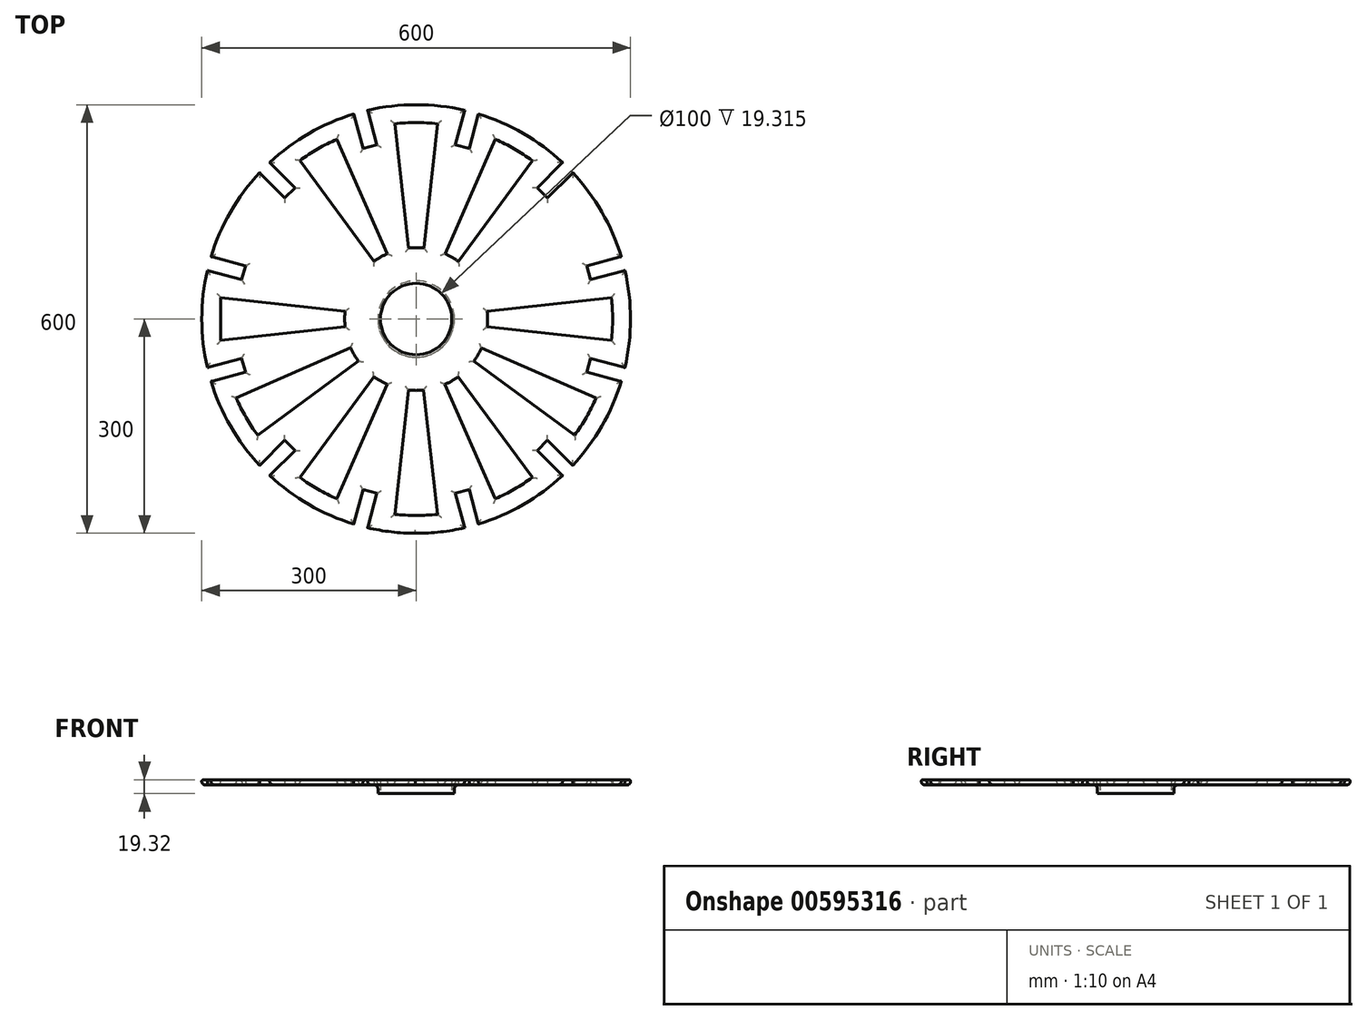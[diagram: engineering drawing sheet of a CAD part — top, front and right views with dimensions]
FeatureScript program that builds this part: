
annotation { "Feature Type Name" : "Feature", "Feature Type Description" : "" }
export const myFeature = defineFeature(function(context is Context, id is Id, definition is map)
    precondition{}
    {
        {
            var Q0;
            Q0=qCreatedBy(makeId("Right.planeOp"),FACE);
            var sketch = newSketch(context, id + "F0", { "sketchPlane" : qUnion([Q0])});
            skLineSegment(sketch, "E0.bottom", {"start": v(0, 0) * mm, "end": v(-300, 0) * mm});
            skLineSegment(sketch, "E0.top", {"start": v(0, 7) * mm, "end": v(-300, 7) * mm});
            skLineSegment(sketch, "E0.left", {"start": v(0, 0) * mm, "end": v(0, 7) * mm});
            skLineSegment(sketch, "E0.right", {"start": v(-300, 0) * mm, "end": v(-300, 7) * mm});
            skSolve(sketch);
        }
        {
            var Q0;
            Q0=makeQuery(id+"F0.imprint","IMPRINT",FACE,{"disambiguationData":[TD([[makeQuery(id+"F0.imprint","IMPRINT",EDGE,{"derivedFrom":sQuery(id+"F0.wireOp",EDGE,"E0.bottom")}),-1.0]])]});
            extrude(context, id + "F1", {"entities" : qUnion([Q0]), "oppositeDirection" : true, "depth" : 1 * mm, "offsetDistance" : 25 * mm});
        }
        {
            var Q0;
            Q0=qCreatedBy(makeId("Right.planeOp"),FACE);
            var sketch = newSketch(context, id + "F2", { "sketchPlane" : qUnion([Q0])});
            skLineSegment(sketch, "E1", {"start": v(-250.92, 0) * mm, "end": v(-210.92, 0) * mm});
            skLineSegment(sketch, "E2", {"start": v(-250.92, 0) * mm, "end": v(-250.92, 7.32) * mm});
            skLineSegment(sketch, "E3", {"start": v(-250.92, 7.32) * mm, "end": v(-210.92, 7.32) * mm});
            skLineSegment(sketch, "E4", {"start": v(-210.92, 7.32) * mm, "end": v(-210.92, 0) * mm});
            skLineSegment(sketch, "E5", {"start": v(0, 0) * mm, "end": v(-300, 0) * mm});
            skLineSegment(sketch, "E6", {"start": v(-300, 0) * mm, "end": v(-300, 7.32) * mm});
            skLineSegment(sketch, "E7", {"start": v(-300, 7.32) * mm, "end": v(0, 7.32) * mm});
            skLineSegment(sketch, "E8", {"start": v(0, 7.32) * mm, "end": v(0, 0) * mm});
            skSolve(sketch);
        }
        {
            var Q0;
            {var subQ0=sQuery(id+"F2.wireOp",EDGE,"E2");Q0=makeQuery(id+"F2.imprint","IMPRINT",FACE,{"disambiguationData":[TD([[makeQuery(id+"F2.imprint","IMPRINT",EDGE,{"derivedFrom":subQ0}),1.0]])]});}
            var Q1;
            {var subQ0=sQuery(id+"F2.wireOp",EDGE,"E4");Q1=makeQuery(id+"F2.imprint","IMPRINT",FACE,{"disambiguationData":[TD([[makeQuery(id+"F2.imprint","IMPRINT",EDGE,{"derivedFrom":subQ0}),1.0]])]});}
            var Q2;
            {var subQ0=sQuery(id+"F2.wireOp",EDGE,"E2");Q2=makeQuery(id+"F2.imprint","IMPRINT",FACE,{"disambiguationData":[TD([[makeQuery(id+"F2.imprint","IMPRINT",EDGE,{"derivedFrom":subQ0}),-1.0]])]});}
            var Q3;
            Q3=sQuery(id+"F2.wireOp",EDGE,"E8");
            revolve(context, id + "F3", {"operationType" : NewBodyOperationType.ADD, "entities" : qUnion([Q0, Q1, Q2]), "axis" : qUnion([Q3]), "revolveType" : RevolveType.FULL});
        }
        {
            var Q0;
            Q0=makeQuery(id+"F3.opRevolve","SWEPT_EDGE",EDGE,{"disambiguationData":[OSD([sQuery(id+"F2.wireOp",EDGE,"E6"),sQuery(id+"F2.wireOp",EDGE,"E7")])]});
            fillet(context, id + "F4", {"entities" : qUnion([Q0]), "radius" : 2 * mm, "tangentPropagation" : true, "allowEdgeOverflow" : false});
        }
        {
            var Q0;
            Q0=qCreatedBy(makeId("Top.planeOp"),FACE);
            var sketch = newSketch(context, id + "F5", { "sketchPlane" : qUnion([Q0])});
            skCircle(sketch, "E9.cCircle", {"center": v(0, 0) * mm, "radius": 300.17 * mm, "construction": true});
            skLineSegment(sketch, "E9.0", {"start": v(80.43, -300.17) * mm, "end": v(-80.43, -300.17) * mm});
            skLineSegment(sketch, "E9.1", {"start": v(-80.43, -300.17) * mm, "end": v(-219.74, -219.74) * mm});
            skLineSegment(sketch, "E9.2", {"start": v(-219.74, -219.74) * mm, "end": v(-300.17, -80.43) * mm});
            skLineSegment(sketch, "E9.3", {"start": v(-300.17, -80.43) * mm, "end": v(-300.17, 80.43) * mm});
            skLineSegment(sketch, "E9.4", {"start": v(-300.17, 80.43) * mm, "end": v(-219.74, 219.74) * mm});
            skLineSegment(sketch, "E9.5", {"start": v(-219.74, 219.74) * mm, "end": v(-80.43, 300.17) * mm});
            skLineSegment(sketch, "E9.6", {"start": v(-80.43, 300.17) * mm, "end": v(80.43, 300.17) * mm});
            skLineSegment(sketch, "E9.7", {"start": v(80.43, 300.17) * mm, "end": v(219.74, 219.74) * mm});
            skLineSegment(sketch, "E9.8", {"start": v(219.74, 219.74) * mm, "end": v(300.17, 80.43) * mm});
            skLineSegment(sketch, "E9.9", {"start": v(300.17, 80.43) * mm, "end": v(300.17, -80.43) * mm});
            skLineSegment(sketch, "E9.10", {"start": v(300.17, -80.43) * mm, "end": v(219.74, -219.74) * mm});
            skLineSegment(sketch, "E9.11", {"start": v(219.74, -219.74) * mm, "end": v(80.43, -300.17) * mm});
            skLineSegment(sketch, "E10", {"start": v(-80.43, -300.17) * mm, "end": v(80.43, 300.17) * mm});
            skLineSegment(sketch, "E11", {"start": v(-80.43, 300.17) * mm, "end": v(80.43, -300.17) * mm});
            skLineSegment(sketch, "E12", {"start": v(219.74, -219.74) * mm, "end": v(-219.74, 219.74) * mm});
            skLineSegment(sketch, "E13", {"start": v(219.74, 219.74) * mm, "end": v(-219.74, -219.74) * mm});
            skLineSegment(sketch, "E14", {"start": v(-300.17, -80.43) * mm, "end": v(300.17, 80.43) * mm});
            skLineSegment(sketch, "E15", {"start": v(300.17, -80.43) * mm, "end": v(-300.17, 80.43) * mm});
            skLineSegment(sketch, "E16", {"start": v(-87.3, 287.19) * mm, "end": v(-67.99, 292.37) * mm});
            skLineSegment(sketch, "E17", {"start": v(-87.3, 287.19) * mm, "end": v(-74.36, 238.9) * mm});
            skLineSegment(sketch, "E18", {"start": v(-74.36, 238.9) * mm, "end": v(-55.05, 244.07) * mm});
            skLineSegment(sketch, "E19", {"start": v(-55.05, 244.07) * mm, "end": v(-67.99, 292.37) * mm});
            skLineSegment(sketch, "E20.1.0", {"start": v(67.99, 292.37) * mm, "end": v(55.05, 244.07) * mm});
            skLineSegment(sketch, "E20.1.1", {"start": v(74.36, 238.9) * mm, "end": v(87.3, 287.19) * mm});
            skLineSegment(sketch, "E20.1.2", {"start": v(55.05, 244.07) * mm, "end": v(74.36, 238.9) * mm});
            skLineSegment(sketch, "E20.1.3", {"start": v(67.99, 292.37) * mm, "end": v(87.3, 287.19) * mm});
            skLineSegment(sketch, "E20.2.0", {"start": v(205.06, 219.2) * mm, "end": v(169.7, 183.85) * mm});
            skLineSegment(sketch, "E20.2.1", {"start": v(183.85, 169.7) * mm, "end": v(219.2, 205.06) * mm});
            skLineSegment(sketch, "E20.2.2", {"start": v(169.7, 183.85) * mm, "end": v(183.85, 169.7) * mm});
            skLineSegment(sketch, "E20.2.3", {"start": v(205.06, 219.2) * mm, "end": v(219.2, 205.06) * mm});
            skLineSegment(sketch, "E20.3.0", {"start": v(287.19, 87.3) * mm, "end": v(238.9, 74.36) * mm});
            skLineSegment(sketch, "E20.3.1", {"start": v(244.07, 55.05) * mm, "end": v(292.37, 67.99) * mm});
            skLineSegment(sketch, "E20.3.2", {"start": v(238.9, 74.36) * mm, "end": v(244.07, 55.05) * mm});
            skLineSegment(sketch, "E20.3.3", {"start": v(287.19, 87.3) * mm, "end": v(292.37, 67.99) * mm});
            skLineSegment(sketch, "E20.4.0", {"start": v(292.37, -67.99) * mm, "end": v(244.07, -55.05) * mm});
            skLineSegment(sketch, "E20.4.1", {"start": v(238.9, -74.36) * mm, "end": v(287.19, -87.3) * mm});
            skLineSegment(sketch, "E20.4.2", {"start": v(244.07, -55.05) * mm, "end": v(238.9, -74.36) * mm});
            skLineSegment(sketch, "E20.4.3", {"start": v(292.37, -67.99) * mm, "end": v(287.19, -87.3) * mm});
            skLineSegment(sketch, "E20.5.0", {"start": v(219.2, -205.06) * mm, "end": v(183.85, -169.7) * mm});
            skLineSegment(sketch, "E20.5.1", {"start": v(169.7, -183.85) * mm, "end": v(205.06, -219.2) * mm});
            skLineSegment(sketch, "E20.5.2", {"start": v(183.85, -169.7) * mm, "end": v(169.7, -183.85) * mm});
            skLineSegment(sketch, "E20.5.3", {"start": v(219.2, -205.06) * mm, "end": v(205.06, -219.2) * mm});
            skLineSegment(sketch, "E20.6.0", {"start": v(87.3, -287.19) * mm, "end": v(74.36, -238.9) * mm});
            skLineSegment(sketch, "E20.6.1", {"start": v(55.05, -244.07) * mm, "end": v(67.99, -292.37) * mm});
            skLineSegment(sketch, "E20.6.2", {"start": v(74.36, -238.9) * mm, "end": v(55.05, -244.07) * mm});
            skLineSegment(sketch, "E20.6.3", {"start": v(87.3, -287.19) * mm, "end": v(67.99, -292.37) * mm});
            skLineSegment(sketch, "E20.7.0", {"start": v(-67.99, -292.37) * mm, "end": v(-55.05, -244.07) * mm});
            skLineSegment(sketch, "E20.7.1", {"start": v(-74.36, -238.9) * mm, "end": v(-87.3, -287.19) * mm});
            skLineSegment(sketch, "E20.7.2", {"start": v(-55.05, -244.07) * mm, "end": v(-74.36, -238.9) * mm});
            skLineSegment(sketch, "E20.7.3", {"start": v(-67.99, -292.37) * mm, "end": v(-87.3, -287.19) * mm});
            skLineSegment(sketch, "E20.8.0", {"start": v(-205.06, -219.2) * mm, "end": v(-169.7, -183.85) * mm});
            skLineSegment(sketch, "E20.8.1", {"start": v(-183.85, -169.7) * mm, "end": v(-219.2, -205.06) * mm});
            skLineSegment(sketch, "E20.8.2", {"start": v(-169.7, -183.85) * mm, "end": v(-183.85, -169.7) * mm});
            skLineSegment(sketch, "E20.8.3", {"start": v(-205.06, -219.2) * mm, "end": v(-219.2, -205.06) * mm});
            skLineSegment(sketch, "E20.9.0", {"start": v(-287.19, -87.3) * mm, "end": v(-238.9, -74.36) * mm});
            skLineSegment(sketch, "E20.9.1", {"start": v(-244.07, -55.05) * mm, "end": v(-292.37, -67.99) * mm});
            skLineSegment(sketch, "E20.9.2", {"start": v(-238.9, -74.36) * mm, "end": v(-244.07, -55.05) * mm});
            skLineSegment(sketch, "E20.9.3", {"start": v(-287.19, -87.3) * mm, "end": v(-292.37, -67.99) * mm});
            skLineSegment(sketch, "E20.10.0", {"start": v(-292.37, 67.99) * mm, "end": v(-244.07, 55.05) * mm});
            skLineSegment(sketch, "E20.10.1", {"start": v(-238.9, 74.36) * mm, "end": v(-287.19, 87.3) * mm});
            skLineSegment(sketch, "E20.10.2", {"start": v(-244.07, 55.05) * mm, "end": v(-238.9, 74.36) * mm});
            skLineSegment(sketch, "E20.10.3", {"start": v(-292.37, 67.99) * mm, "end": v(-287.19, 87.3) * mm});
            skLineSegment(sketch, "E20.11.0", {"start": v(-219.2, 205.06) * mm, "end": v(-183.85, 169.7) * mm});
            skLineSegment(sketch, "E20.11.1", {"start": v(-169.7, 183.85) * mm, "end": v(-205.06, 219.2) * mm});
            skLineSegment(sketch, "E20.11.2", {"start": v(-183.85, 169.7) * mm, "end": v(-169.7, 183.85) * mm});
            skLineSegment(sketch, "E20.11.3", {"start": v(-219.2, 205.06) * mm, "end": v(-205.06, 219.2) * mm});
            skLineSegment(sketch, "E20.anchor1", {"start": v(0, 0) * mm, "end": v(-74.36, 238.9) * mm, "construction": true});
            skLineSegment(sketch, "E20.anchor2", {"start": v(0, 0) * mm, "end": v(-183.85, 169.7) * mm, "construction": true});
            skSolve(sketch);
        }
        {
            var Q0;
            {var subQ5=sQuery(id+"F5.wireOp",EDGE,"E20.9.0");Q0=makeQuery(id+"F5.imprint","IMPRINT",FACE,{"disambiguationData":[TD([[makeQuery(id+"F5.imprint","IMPRINT",EDGE,{"derivedFrom":subQ5}),1.0]])]});}
            var Q1;
            {var subQ5=sQuery(id+"F5.wireOp",EDGE,"E20.9.1");Q1=makeQuery(id+"F5.imprint","IMPRINT",FACE,{"disambiguationData":[TD([[makeQuery(id+"F5.imprint","IMPRINT",EDGE,{"derivedFrom":subQ5}),1.0]])]});}
            var Q2;
            {var subQ5=sQuery(id+"F5.wireOp",EDGE,"E20.8.1");Q2=makeQuery(id+"F5.imprint","IMPRINT",FACE,{"disambiguationData":[TD([[makeQuery(id+"F5.imprint","IMPRINT",EDGE,{"derivedFrom":subQ5}),1.0]])]});}
            var Q3;
            {var subQ5=sQuery(id+"F5.wireOp",EDGE,"E20.8.0");Q3=makeQuery(id+"F5.imprint","IMPRINT",FACE,{"disambiguationData":[TD([[makeQuery(id+"F5.imprint","IMPRINT",EDGE,{"derivedFrom":subQ5}),1.0]])]});}
            var Q4;
            {var subQ5=sQuery(id+"F5.wireOp",EDGE,"E20.7.1");Q4=makeQuery(id+"F5.imprint","IMPRINT",FACE,{"disambiguationData":[TD([[makeQuery(id+"F5.imprint","IMPRINT",EDGE,{"derivedFrom":subQ5}),1.0]])]});}
            var Q5;
            {var subQ5=sQuery(id+"F5.wireOp",EDGE,"E20.7.0");Q5=makeQuery(id+"F5.imprint","IMPRINT",FACE,{"disambiguationData":[TD([[makeQuery(id+"F5.imprint","IMPRINT",EDGE,{"derivedFrom":subQ5}),1.0]])]});}
            var Q6;
            {var subQ5=sQuery(id+"F5.wireOp",EDGE,"E20.6.1");Q6=makeQuery(id+"F5.imprint","IMPRINT",FACE,{"disambiguationData":[TD([[makeQuery(id+"F5.imprint","IMPRINT",EDGE,{"derivedFrom":subQ5}),1.0]])]});}
            var Q7;
            {var subQ5=sQuery(id+"F5.wireOp",EDGE,"E20.6.0");Q7=makeQuery(id+"F5.imprint","IMPRINT",FACE,{"disambiguationData":[TD([[makeQuery(id+"F5.imprint","IMPRINT",EDGE,{"derivedFrom":subQ5}),1.0]])]});}
            var Q8;
            {var subQ5=sQuery(id+"F5.wireOp",EDGE,"E20.5.1");Q8=makeQuery(id+"F5.imprint","IMPRINT",FACE,{"disambiguationData":[TD([[makeQuery(id+"F5.imprint","IMPRINT",EDGE,{"derivedFrom":subQ5}),1.0]])]});}
            var Q9;
            {var subQ5=sQuery(id+"F5.wireOp",EDGE,"E20.5.0");Q9=makeQuery(id+"F5.imprint","IMPRINT",FACE,{"disambiguationData":[TD([[makeQuery(id+"F5.imprint","IMPRINT",EDGE,{"derivedFrom":subQ5}),1.0]])]});}
            var Q10;
            {var subQ5=sQuery(id+"F5.wireOp",EDGE,"E20.4.1");Q10=makeQuery(id+"F5.imprint","IMPRINT",FACE,{"disambiguationData":[TD([[makeQuery(id+"F5.imprint","IMPRINT",EDGE,{"derivedFrom":subQ5}),1.0]])]});}
            var Q11;
            {var subQ5=sQuery(id+"F5.wireOp",EDGE,"E20.4.0");Q11=makeQuery(id+"F5.imprint","IMPRINT",FACE,{"disambiguationData":[TD([[makeQuery(id+"F5.imprint","IMPRINT",EDGE,{"derivedFrom":subQ5}),1.0]])]});}
            var Q12;
            {var subQ5=sQuery(id+"F5.wireOp",EDGE,"E20.3.1");Q12=makeQuery(id+"F5.imprint","IMPRINT",FACE,{"disambiguationData":[TD([[makeQuery(id+"F5.imprint","IMPRINT",EDGE,{"derivedFrom":subQ5}),1.0]])]});}
            var Q13;
            {var subQ5=sQuery(id+"F5.wireOp",EDGE,"E20.3.0");Q13=makeQuery(id+"F5.imprint","IMPRINT",FACE,{"disambiguationData":[TD([[makeQuery(id+"F5.imprint","IMPRINT",EDGE,{"derivedFrom":subQ5}),1.0]])]});}
            var Q14;
            {var subQ5=sQuery(id+"F5.wireOp",EDGE,"E20.2.1");Q14=makeQuery(id+"F5.imprint","IMPRINT",FACE,{"disambiguationData":[TD([[makeQuery(id+"F5.imprint","IMPRINT",EDGE,{"derivedFrom":subQ5}),1.0]])]});}
            var Q15;
            {var subQ5=sQuery(id+"F5.wireOp",EDGE,"E20.2.0");Q15=makeQuery(id+"F5.imprint","IMPRINT",FACE,{"disambiguationData":[TD([[makeQuery(id+"F5.imprint","IMPRINT",EDGE,{"derivedFrom":subQ5}),1.0]])]});}
            var Q16;
            {var subQ5=sQuery(id+"F5.wireOp",EDGE,"E20.1.1");Q16=makeQuery(id+"F5.imprint","IMPRINT",FACE,{"disambiguationData":[TD([[makeQuery(id+"F5.imprint","IMPRINT",EDGE,{"derivedFrom":subQ5}),1.0]])]});}
            var Q17;
            {var subQ5=sQuery(id+"F5.wireOp",EDGE,"E20.1.0");Q17=makeQuery(id+"F5.imprint","IMPRINT",FACE,{"disambiguationData":[TD([[makeQuery(id+"F5.imprint","IMPRINT",EDGE,{"derivedFrom":subQ5}),1.0]])]});}
            var Q18;
            {var subQ5=sQuery(id+"F5.wireOp",EDGE,"E19");Q18=makeQuery(id+"F5.imprint","IMPRINT",FACE,{"disambiguationData":[TD([[makeQuery(id+"F5.imprint","IMPRINT",EDGE,{"derivedFrom":subQ5}),1.0]])]});}
            var Q19;
            {var subQ5=sQuery(id+"F5.wireOp",EDGE,"E17");Q19=makeQuery(id+"F5.imprint","IMPRINT",FACE,{"disambiguationData":[TD([[makeQuery(id+"F5.imprint","IMPRINT",EDGE,{"derivedFrom":subQ5}),1.0]])]});}
            var Q20;
            {var subQ5=sQuery(id+"F5.wireOp",EDGE,"E20.11.1");Q20=makeQuery(id+"F5.imprint","IMPRINT",FACE,{"disambiguationData":[TD([[makeQuery(id+"F5.imprint","IMPRINT",EDGE,{"derivedFrom":subQ5}),1.0]])]});}
            var Q21;
            {var subQ5=sQuery(id+"F5.wireOp",EDGE,"E20.11.0");Q21=makeQuery(id+"F5.imprint","IMPRINT",FACE,{"disambiguationData":[TD([[makeQuery(id+"F5.imprint","IMPRINT",EDGE,{"derivedFrom":subQ5}),1.0]])]});}
            var Q22;
            {var subQ5=sQuery(id+"F5.wireOp",EDGE,"E20.10.1");Q22=makeQuery(id+"F5.imprint","IMPRINT",FACE,{"disambiguationData":[TD([[makeQuery(id+"F5.imprint","IMPRINT",EDGE,{"derivedFrom":subQ5}),1.0]])]});}
            var Q23;
            {var subQ5=sQuery(id+"F5.wireOp",EDGE,"E20.10.0");Q23=makeQuery(id+"F5.imprint","IMPRINT",FACE,{"disambiguationData":[TD([[makeQuery(id+"F5.imprint","IMPRINT",EDGE,{"derivedFrom":subQ5}),1.0]])]});}
            extrude(context, id + "F6", {"entities" : qUnion([Q0, Q1, Q2, Q3, Q4, Q5, Q6, Q7, Q8, Q9, Q10, Q11, Q12, Q13, Q14, Q15, Q16, Q17, Q18, Q19, Q20, Q21, Q22, Q23]), "operationType" : NewBodyOperationType.REMOVE, "depth" : 10 * mm, "offsetDistance" : 25 * mm});
        }
        {
            var Q0;
            Q0=qCreatedBy(makeId("Top.planeOp"),FACE);
            var sketch = newSketch(context, id + "F7", { "sketchPlane" : qUnion([Q0])});
            skCircle(sketch, "E21", {"center": v(0, 0) * mm, "radius": 50 * mm});
            skCircle(sketch, "E22", {"center": v(0, 0) * mm, "radius": 53.5 * mm});
            skSolve(sketch);
        }
        {
            var Q0;
            Q0=makeQuery(id+"F7.imprint","IMPRINT",FACE,{"disambiguationData":[TD([[makeQuery(id+"F7.imprint","IMPRINT",EDGE,{"derivedFrom":sQuery(id+"F7.wireOp",EDGE,"E21")}),1.0]])]});
            extrude(context, id + "F8", {"entities" : qUnion([Q0]), "operationType" : NewBodyOperationType.REMOVE, "depth" : 25 * mm, "offsetDistance" : 25 * mm});
        }
        {
            var Q0;
            Q0=makeQuery(id+"F3.boolean.opBoolean","MERGE",FACE,{"derivedFrom":[makeQuery(id+"F1.opExtrude","SWEPT_FACE",FACE,{"disambiguationData":[OSD([sQuery(id+"F0.wireOp",EDGE,"E0.bottom")])]}),makeQuery(id+"F3.opRevolve","SWEPT_FACE",FACE,{"disambiguationData":[OSD([sQuery(id+"F2.wireOp",EDGE,"E5")])]})]});
            var sketch = newSketch(context, id + "F9", { "sketchPlane" : qUnion([Q0])});
            skCircle(sketch, "E23", {"center": v(0, 0) * mm, "radius": 53.5 * mm});
            skSolve(sketch);
        }
        {
            var Q0;
            Q0=makeQuery(id+"F9.imprint","IMPRINT",FACE,{"disambiguationData":[TD([[makeQuery(id+"F9.imprint","IMPRINT",EDGE,{"derivedFrom":sQuery(id+"F9.wireOp",EDGE,"E23")}),1.0]])]});
            extrude(context, id + "F10", {"entities" : qUnion([Q0]), "operationType" : NewBodyOperationType.ADD, "depth" : 12 * mm, "offsetDistance" : 25 * mm});
        }
        {
            var Q0;
            Q0=qCreatedBy(makeId("Top.planeOp"),FACE);
            var sketch = newSketch(context, id + "F11", { "sketchPlane" : qUnion([Q0])});
            skCircle(sketch, "E24", {"center": v(0, 0) * mm, "radius": 275 * mm});
            skPoint(sketch, "E25", {"position": v(267.8, -62.55) * mm});
            skPoint(sketch, "E26", {"position": v(268.2, 60.82) * mm});
            skCircle(sketch, "E27", {"center": v(0, 0) * mm, "radius": 100 * mm});
            skLineSegment(sketch, "E28", {"start": v(268.2, 60.82) * mm, "end": v(273.22, 31.24) * mm});
            skLineSegment(sketch, "E29", {"start": v(273.22, 31.24) * mm, "end": v(-273.36, -30) * mm});
            skLineSegment(sketch, "E30", {"start": v(-273.36, -30) * mm, "end": v(-273.36, 30) * mm});
            skLineSegment(sketch, "E31", {"start": v(-273.36, 30) * mm, "end": v(273.37, -29.87) * mm});
            skArc(sketch, "E32", {"start": v(273.37, -29.87) * mm, "mid": v(275.84, 0.7) * mm, "end": v(273.22, 31.24) * mm});
            skPoint(sketch, "E33", {"position": v(99.3, 11.76) * mm});
            skPoint(sketch, "E34", {"position": v(99.41, -10.82) * mm});
            skPoint(sketch, "E35", {"position": v(-99.45, -10.51) * mm});
            skPoint(sketch, "E36", {"position": v(-99.4, 10.95) * mm});
            skPoint(sketch, "E37", {"position": v(-273.36, -30) * mm});
            skPoint(sketch, "E38", {"position": v(-273.36, 30) * mm});
            skLineSegment(sketch, "E39.1.0", {"start": v(-251.74, -110.7) * mm, "end": v(251.68, 110.82) * mm});
            skLineSegment(sketch, "E39.1.1", {"start": v(221, 163.67) * mm, "end": v(-221.74, -162.66) * mm});
            skLineSegment(sketch, "E39.2.0", {"start": v(-162.66, -221.74) * mm, "end": v(162.55, 221.81) * mm});
            skLineSegment(sketch, "E39.2.1", {"start": v(109.55, 252.24) * mm, "end": v(-110.7, -251.74) * mm});
            skLineSegment(sketch, "E39.3.0", {"start": v(-30, -273.36) * mm, "end": v(29.87, 273.37) * mm});
            skLineSegment(sketch, "E39.3.1", {"start": v(-31.24, 273.22) * mm, "end": v(30, -273.36) * mm});
            skLineSegment(sketch, "E39.4.0", {"start": v(110.7, -251.74) * mm, "end": v(-110.82, 251.68) * mm});
            skLineSegment(sketch, "E39.4.1", {"start": v(-163.67, 221) * mm, "end": v(162.66, -221.74) * mm});
            skLineSegment(sketch, "E39.5.0", {"start": v(221.74, -162.66) * mm, "end": v(-221.81, 162.55) * mm});
            skLineSegment(sketch, "E39.5.1", {"start": v(-252.24, 109.55) * mm, "end": v(251.74, -110.7) * mm});
            skLineSegment(sketch, "E39.6.0", {"start": v(273.36, -30) * mm, "end": v(-273.37, 29.87) * mm});
            skLineSegment(sketch, "E39.6.1", {"start": v(-273.22, -31.24) * mm, "end": v(273.36, 30) * mm});
            skLineSegment(sketch, "E39.7.0", {"start": v(251.74, 110.7) * mm, "end": v(-251.68, -110.82) * mm});
            skLineSegment(sketch, "E39.7.1", {"start": v(-221, -163.67) * mm, "end": v(221.74, 162.66) * mm});
            skLineSegment(sketch, "E39.8.0", {"start": v(162.66, 221.74) * mm, "end": v(-162.55, -221.81) * mm});
            skLineSegment(sketch, "E39.8.1", {"start": v(-109.55, -252.24) * mm, "end": v(110.7, 251.74) * mm});
            skLineSegment(sketch, "E39.9.0", {"start": v(30, 273.36) * mm, "end": v(-29.87, -273.37) * mm});
            skLineSegment(sketch, "E39.9.1", {"start": v(31.24, -273.22) * mm, "end": v(-30, 273.36) * mm});
            skLineSegment(sketch, "E39.10.0", {"start": v(-110.7, 251.74) * mm, "end": v(110.82, -251.68) * mm});
            skLineSegment(sketch, "E39.10.1", {"start": v(163.67, -221) * mm, "end": v(-162.66, 221.74) * mm});
            skLineSegment(sketch, "E39.11.0", {"start": v(-221.74, 162.66) * mm, "end": v(221.81, -162.55) * mm});
            skLineSegment(sketch, "E39.11.1", {"start": v(252.24, -109.55) * mm, "end": v(-251.74, 110.7) * mm});
            skSolve(sketch);
        }
        {
            var Q0;
            {var subQ5=sQuery(id+"F11.wireOp",EDGE,"E30");Q0=makeQuery(id+"F11.imprint","IMPRINT",FACE,{"disambiguationData":[TD([[makeQuery(id+"F11.imprint","IMPRINT",EDGE,{"derivedFrom":subQ5}),-1.0]])]});}
            var Q1;
            {var subQ1=sQuery(id+"F11.wireOp",EDGE,"E29");var subQ6=sQuery(id+"F11.wireOp",EDGE,"E27");var subQ7=makeQuery(id+"F11.imprint","INTERSECT",VERTEX,{"disambiguationData":[OD(0.0)],"derivedFrom":[subQ6,subQ1]});Q1=makeQuery(id+"F11.imprint","IMPRINT",FACE,{"disambiguationData":[TD([[makeQuery(id+"F11.imprint","IMPRINT",EDGE,{"disambiguationData":[TD([[subQ7,1.0]])],"derivedFrom":subQ6}),-1.0]])]});}
            var Q2;
            {var subQ3=sQuery(id+"F11.wireOp",EDGE,"E39.6.1");var subQ5=sQuery(id+"F11.wireOp",EDGE,"E27");var subQ6=makeQuery(id+"F11.imprint","INTERSECT",VERTEX,{"disambiguationData":[OD(0.0)],"derivedFrom":[subQ5,subQ3]});Q2=makeQuery(id+"F11.imprint","IMPRINT",FACE,{"disambiguationData":[TD([[makeQuery(id+"F11.imprint","IMPRINT",EDGE,{"disambiguationData":[TD([[subQ6,1.0]])],"derivedFrom":subQ5}),-1.0]])]});}
            var Q3;
            {var subQ0=sQuery(id+"F11.wireOp",EDGE,"E39.5.0");var subQ1=sQuery(id+"F11.wireOp",EDGE,"E24");var subQ2=makeQuery(id+"F11.imprint","INTERSECT",VERTEX,{"disambiguationData":[OD(1.0)],"derivedFrom":[subQ1,subQ0]});Q3=makeQuery(id+"F11.imprint","IMPRINT",FACE,{"disambiguationData":[TD([[makeQuery(id+"F11.imprint","IMPRINT",EDGE,{"disambiguationData":[TD([[subQ2,-1.0]])],"derivedFrom":subQ1}),1.0]])]});}
            var Q4;
            {var subQ0=sQuery(id+"F11.wireOp",EDGE,"E39.4.0");var subQ1=sQuery(id+"F11.wireOp",EDGE,"E24");var subQ2=makeQuery(id+"F11.imprint","INTERSECT",VERTEX,{"disambiguationData":[OD(1.0)],"derivedFrom":[subQ1,subQ0]});Q4=makeQuery(id+"F11.imprint","IMPRINT",FACE,{"disambiguationData":[TD([[makeQuery(id+"F11.imprint","IMPRINT",EDGE,{"disambiguationData":[TD([[subQ2,-1.0]])],"derivedFrom":subQ1}),1.0]])]});}
            var Q5;
            {var subQ0=sQuery(id+"F11.wireOp",EDGE,"E39.3.0");var subQ1=sQuery(id+"F11.wireOp",EDGE,"E24");var subQ2=makeQuery(id+"F11.imprint","INTERSECT",VERTEX,{"disambiguationData":[OD(1.0)],"derivedFrom":[subQ1,subQ0]});Q5=makeQuery(id+"F11.imprint","IMPRINT",FACE,{"disambiguationData":[TD([[makeQuery(id+"F11.imprint","IMPRINT",EDGE,{"disambiguationData":[TD([[subQ2,-1.0]])],"derivedFrom":subQ1}),1.0]])]});}
            var Q6;
            {var subQ0=sQuery(id+"F11.wireOp",EDGE,"E39.2.0");var subQ1=sQuery(id+"F11.wireOp",EDGE,"E24");var subQ2=makeQuery(id+"F11.imprint","INTERSECT",VERTEX,{"disambiguationData":[OD(1.0)],"derivedFrom":[subQ1,subQ0]});Q6=makeQuery(id+"F11.imprint","IMPRINT",FACE,{"disambiguationData":[TD([[makeQuery(id+"F11.imprint","IMPRINT",EDGE,{"disambiguationData":[TD([[subQ2,-1.0]])],"derivedFrom":subQ1}),1.0]])]});}
            var Q7;
            {var subQ0=sQuery(id+"F11.wireOp",EDGE,"E39.1.0");var subQ1=sQuery(id+"F11.wireOp",EDGE,"E24");var subQ2=makeQuery(id+"F11.imprint","INTERSECT",VERTEX,{"disambiguationData":[OD(1.0)],"derivedFrom":[subQ1,subQ0]});Q7=makeQuery(id+"F11.imprint","IMPRINT",FACE,{"disambiguationData":[TD([[makeQuery(id+"F11.imprint","IMPRINT",EDGE,{"disambiguationData":[TD([[subQ2,-1.0]])],"derivedFrom":subQ1}),1.0]])]});}
            var Q8;
            {var subQ0=sQuery(id+"F11.wireOp",EDGE,"E39.5.1");var subQ1=sQuery(id+"F11.wireOp",EDGE,"E24");var subQ2=makeQuery(id+"F11.imprint","INTERSECT",VERTEX,{"disambiguationData":[OD(1.0)],"derivedFrom":[subQ1,subQ0]});Q8=makeQuery(id+"F11.imprint","IMPRINT",FACE,{"disambiguationData":[TD([[makeQuery(id+"F11.imprint","IMPRINT",EDGE,{"disambiguationData":[TD([[subQ2,1.0]])],"derivedFrom":subQ1}),1.0]])]});}
            var Q9;
            {var subQ0=sQuery(id+"F11.wireOp",EDGE,"E39.4.1");var subQ1=sQuery(id+"F11.wireOp",EDGE,"E24");var subQ2=makeQuery(id+"F11.imprint","INTERSECT",VERTEX,{"disambiguationData":[OD(1.0)],"derivedFrom":[subQ1,subQ0]});Q9=makeQuery(id+"F11.imprint","IMPRINT",FACE,{"disambiguationData":[TD([[makeQuery(id+"F11.imprint","IMPRINT",EDGE,{"disambiguationData":[TD([[subQ2,1.0]])],"derivedFrom":subQ1}),1.0]])]});}
            var Q10;
            {var subQ0=sQuery(id+"F11.wireOp",EDGE,"E39.3.1");var subQ1=sQuery(id+"F11.wireOp",EDGE,"E24");var subQ2=makeQuery(id+"F11.imprint","INTERSECT",VERTEX,{"disambiguationData":[OD(1.0)],"derivedFrom":[subQ1,subQ0]});Q10=makeQuery(id+"F11.imprint","IMPRINT",FACE,{"disambiguationData":[TD([[makeQuery(id+"F11.imprint","IMPRINT",EDGE,{"disambiguationData":[TD([[subQ2,1.0]])],"derivedFrom":subQ1}),1.0]])]});}
            var Q11;
            {var subQ0=sQuery(id+"F11.wireOp",EDGE,"E39.2.1");var subQ1=sQuery(id+"F11.wireOp",EDGE,"E24");var subQ2=makeQuery(id+"F11.imprint","INTERSECT",VERTEX,{"disambiguationData":[OD(1.0)],"derivedFrom":[subQ1,subQ0]});Q11=makeQuery(id+"F11.imprint","IMPRINT",FACE,{"disambiguationData":[TD([[makeQuery(id+"F11.imprint","IMPRINT",EDGE,{"disambiguationData":[TD([[subQ2,1.0]])],"derivedFrom":subQ1}),1.0]])]});}
            var Q12;
            {var subQ0=sQuery(id+"F11.wireOp",EDGE,"E39.1.1");var subQ1=sQuery(id+"F11.wireOp",EDGE,"E24");var subQ2=makeQuery(id+"F11.imprint","INTERSECT",VERTEX,{"disambiguationData":[OD(1.0)],"derivedFrom":[subQ1,subQ0]});Q12=makeQuery(id+"F11.imprint","IMPRINT",FACE,{"disambiguationData":[TD([[makeQuery(id+"F11.imprint","IMPRINT",EDGE,{"disambiguationData":[TD([[subQ2,1.0]])],"derivedFrom":subQ1}),1.0]])]});}
            extrude(context, id + "F12", {"entities" : qUnion([Q0, Q1, Q2, Q3, Q4, Q5, Q6, Q7, Q8, Q9, Q10, Q11, Q12]), "operationType" : NewBodyOperationType.REMOVE, "endBound" : BoundingType.SYMMETRIC, "oppositeDirection" : true, "depth" : 25 * mm, "offsetDistance" : 25 * mm});
        }
        {
            var Q0;
            Q0=makeQuery(id+"F12.boolean.opBoolean","INTERSECT",EDGE,{"derivedFrom":[makeQuery(id+"F3.boolean.opBoolean","MERGE",FACE,{"derivedFrom":[makeQuery(id+"F1.opExtrude","SWEPT_FACE",FACE,{"disambiguationData":[OSD([sQuery(id+"F0.wireOp",EDGE,"E0.bottom")])]}),makeQuery(id+"F3.opRevolve","SWEPT_FACE",FACE,{"disambiguationData":[OSD([sQuery(id+"F2.wireOp",EDGE,"E5")])]})]}),makeQuery(id+"F12.opExtrude","SWEPT_FACE",FACE,{"disambiguationData":[OSD([sQuery(id+"F11.wireOp",EDGE,"E39.8.0")])]})]});
            var Q1;
            {var subQ0=sQuery(id+"F11.wireOp",EDGE,"E27");Q1=makeQuery(id+"F12.boolean.opBoolean","INTERSECT",EDGE,{"derivedFrom":[makeQuery(id+"F3.boolean.opBoolean","MERGE",FACE,{"derivedFrom":[makeQuery(id+"F1.opExtrude","SWEPT_FACE",FACE,{"disambiguationData":[OSD([sQuery(id+"F0.wireOp",EDGE,"E0.bottom")])]}),makeQuery(id+"F3.opRevolve","SWEPT_FACE",FACE,{"disambiguationData":[OSD([sQuery(id+"F2.wireOp",EDGE,"E5")])]})]}),makeQuery(id+"F12.opExtrude","SWEPT_FACE",FACE,{"disambiguationData":[OSD([subQ0]),TDD([makeQuery(id+"F11.imprint","IMPRINT",EDGE,{"disambiguationData":[TD([[makeQuery(id+"F11.imprint","INTERSECT",VERTEX,{"disambiguationData":[OD(1.0)],"derivedFrom":[subQ0,sQuery(id+"F11.wireOp",EDGE,"E39.8.0")]}),-1.0]])],"derivedFrom":subQ0})])]})]});}
            var Q2;
            Q2=makeQuery(id+"F12.boolean.opBoolean","INTERSECT",EDGE,{"derivedFrom":[makeQuery(id+"F3.boolean.opBoolean","MERGE",FACE,{"derivedFrom":[makeQuery(id+"F1.opExtrude","SWEPT_FACE",FACE,{"disambiguationData":[OSD([sQuery(id+"F0.wireOp",EDGE,"E0.bottom")])]}),makeQuery(id+"F3.opRevolve","SWEPT_FACE",FACE,{"disambiguationData":[OSD([sQuery(id+"F2.wireOp",EDGE,"E5")])]})]}),makeQuery(id+"F12.opExtrude","SWEPT_FACE",FACE,{"disambiguationData":[OSD([sQuery(id+"F11.wireOp",EDGE,"E39.2.1")])]})]});
            var Q3;
            {var subQ0=sQuery(id+"F11.wireOp",EDGE,"E24");Q3=makeQuery(id+"F12.boolean.opBoolean","INTERSECT",EDGE,{"derivedFrom":[makeQuery(id+"F3.boolean.opBoolean","MERGE",FACE,{"derivedFrom":[makeQuery(id+"F1.opExtrude","SWEPT_FACE",FACE,{"disambiguationData":[OSD([sQuery(id+"F0.wireOp",EDGE,"E0.bottom")])]}),makeQuery(id+"F3.opRevolve","SWEPT_FACE",FACE,{"disambiguationData":[OSD([sQuery(id+"F2.wireOp",EDGE,"E5")])]})]}),makeQuery(id+"F12.opExtrude","SWEPT_FACE",FACE,{"disambiguationData":[OSD([subQ0]),TDD([makeQuery(id+"F11.imprint","IMPRINT",EDGE,{"disambiguationData":[TD([[makeQuery(id+"F11.imprint","INTERSECT",VERTEX,{"disambiguationData":[OD(1.0)],"derivedFrom":[subQ0,sQuery(id+"F11.wireOp",EDGE,"E39.2.1")]}),1.0]])],"derivedFrom":subQ0})])]})]});}
            var Q4;
            Q4=makeQuery(id+"F12.boolean.opBoolean","INTERSECT",EDGE,{"derivedFrom":[makeQuery(id+"F3.boolean.opBoolean","MERGE",FACE,{"derivedFrom":[makeQuery(id+"F1.opExtrude","SWEPT_FACE",FACE,{"disambiguationData":[OSD([sQuery(id+"F0.wireOp",EDGE,"E0.bottom")])]}),makeQuery(id+"F3.opRevolve","SWEPT_FACE",FACE,{"disambiguationData":[OSD([sQuery(id+"F2.wireOp",EDGE,"E5")])]})]}),makeQuery(id+"F12.opExtrude","SWEPT_FACE",FACE,{"disambiguationData":[OSD([sQuery(id+"F11.wireOp",EDGE,"E39.1.1")])]})]});
            var Q5;
            Q5=makeQuery(id+"F12.boolean.opBoolean","INTERSECT",EDGE,{"derivedFrom":[makeQuery(id+"F3.boolean.opBoolean","MERGE",FACE,{"derivedFrom":[makeQuery(id+"F1.opExtrude","SWEPT_FACE",FACE,{"disambiguationData":[OSD([sQuery(id+"F0.wireOp",EDGE,"E0.bottom")])]}),makeQuery(id+"F3.opRevolve","SWEPT_FACE",FACE,{"disambiguationData":[OSD([sQuery(id+"F2.wireOp",EDGE,"E5")])]})]}),makeQuery(id+"F12.opExtrude","SWEPT_FACE",FACE,{"disambiguationData":[OSD([sQuery(id+"F11.wireOp",EDGE,"E39.7.0")])]})]});
            var Q6;
            {var subQ0=sQuery(id+"F11.wireOp",EDGE,"E27");Q6=makeQuery(id+"F12.boolean.opBoolean","INTERSECT",EDGE,{"derivedFrom":[makeQuery(id+"F3.boolean.opBoolean","MERGE",FACE,{"derivedFrom":[makeQuery(id+"F1.opExtrude","SWEPT_FACE",FACE,{"disambiguationData":[OSD([sQuery(id+"F0.wireOp",EDGE,"E0.bottom")])]}),makeQuery(id+"F3.opRevolve","SWEPT_FACE",FACE,{"disambiguationData":[OSD([sQuery(id+"F2.wireOp",EDGE,"E5")])]})]}),makeQuery(id+"F12.opExtrude","SWEPT_FACE",FACE,{"disambiguationData":[OSD([subQ0]),TDD([makeQuery(id+"F11.imprint","IMPRINT",EDGE,{"disambiguationData":[TD([[makeQuery(id+"F11.imprint","INTERSECT",VERTEX,{"disambiguationData":[OD(1.0)],"derivedFrom":[subQ0,sQuery(id+"F11.wireOp",EDGE,"E39.7.0")]}),-1.0]])],"derivedFrom":subQ0})])]})]});}
            var Q7;
            {var subQ0=sQuery(id+"F11.wireOp",EDGE,"E24");Q7=makeQuery(id+"F12.boolean.opBoolean","INTERSECT",EDGE,{"derivedFrom":[makeQuery(id+"F3.boolean.opBoolean","MERGE",FACE,{"derivedFrom":[makeQuery(id+"F1.opExtrude","SWEPT_FACE",FACE,{"disambiguationData":[OSD([sQuery(id+"F0.wireOp",EDGE,"E0.bottom")])]}),makeQuery(id+"F3.opRevolve","SWEPT_FACE",FACE,{"disambiguationData":[OSD([sQuery(id+"F2.wireOp",EDGE,"E5")])]})]}),makeQuery(id+"F12.opExtrude","SWEPT_FACE",FACE,{"disambiguationData":[OSD([subQ0]),TDD([makeQuery(id+"F11.imprint","IMPRINT",EDGE,{"disambiguationData":[TD([[makeQuery(id+"F11.imprint","INTERSECT",VERTEX,{"disambiguationData":[OD(1.0)],"derivedFrom":[subQ0,sQuery(id+"F11.wireOp",EDGE,"E39.1.1")]}),1.0]])],"derivedFrom":subQ0})])]})]});}
            var Q8;
            Q8=makeQuery(id+"F3.boolean.opBoolean","MERGE",FACE,{"derivedFrom":[makeQuery(id+"F1.opExtrude","SWEPT_FACE",FACE,{"disambiguationData":[OSD([sQuery(id+"F0.wireOp",EDGE,"E0.bottom")])]}),makeQuery(id+"F3.opRevolve","SWEPT_FACE",FACE,{"disambiguationData":[OSD([sQuery(id+"F2.wireOp",EDGE,"E5")])]})]});
            fillet(context, id + "F13", {"entities" : qUnion([Q0, Q1, Q2, Q3, Q4, Q5, Q6, Q7, Q8]), "radius" : 5 * mm, "tangentPropagation" : true, "allowEdgeOverflow" : false});
        }
    });
